# Revit family: Endpiece Linear Lightline_63_UN_Surface-Mounted-Pendant_NAL
name_source: partatom
category: Lighting Fixtures
units: mm (PartAtom-declared; Revit-internal decimal feet)

## family parameters
Always vertical = No
Cut with Voids When Loaded = No
Light Source = No
OmniClass Number = 23.80.70.00
OmniClass Title = Lighting
Part Type = Normal
Room Calculation Point = Yes
Round Connector Dimension = Use Diameter
Shared = No
Work Plane-Based = No

## types (57) — shared parameters
Apparent Load = 16 VA
Assembly Code = 63.0
Description = Surface-mounted or pendant luminaire
Geometry = Linear Lightline - Profile Geometry : Profile + Luminaire
IfcExportAs = IfcLightFixtureType
IfcExportType = USERDEFINED
Lamp = LED
Luminaire_Body_Material = PPS Plastic
Luminaire_Cap_Material = PPS Plastic
Manufacturer = Natec Lighting B.V.
Model = Linear Lightline
URL = https://nateclighting.nl
Voltage = 230 V

## per-type parameters (varying)
| type | Lightsource | Wattage Comments |
| Lighting Properties: 35W - 120° - Milky | Linear Lightline - Lightsource : Properties: 35W - 120° - Milky | 35.3391 W |
| Lighting Properties: 35W - 120° | Linear Lightline - Lightsource : Properties: 35W - 120° | 35.4575 W |
| Lighting Properties: 35W - 30° | Linear Lightline - Lightsource : Properties: 35W - 30° | 35.4382 W |
| Lighting Properties: 35W - 60° | Linear Lightline - Lightsource : Properties: 35W - 60° | 35.4888 W |
| Lighting Properties: 35W - 90°. | Linear Lightline - Lightsource : Properties: 35W - 90°. | 35.4593 W |
| Lighting Properties: 35W - Asymmetrisch | Linear Lightline - Lightsource : Properties: 35W - Asymmetrisch | 35.4371 W |
| Lighting Properties: 35W - Dubbel Asymmetrisch | Linear Lightline - Lightsource : Properties: 35W - Dubbel Asymmetrisch | 35.4449 W |
| Lighting Properties: 40W - 120° - Milky | Linear Lightline - Lightsource : Properties: 40W - 120° - Milky | 40.2837 W |
| Lighting Properties: 40W - 120° | Linear Lightline - Lightsource : Properties: 40W - 120° | 40.3964 W |
| Lighting Properties: 40W - 30° | Linear Lightline - Lightsource : Properties: 40W - 30° | 40.4281 W |
| Lighting Properties: 40W - 60° | Linear Lightline - Lightsource : Properties: 40W - 60° | 40.4582 W |
| Lighting Properties: 40W - 90° | Linear Lightline - Lightsource : Properties: 40W - 90° | 40.4791 W |
| Lighting Properties: 40W - Asymmetrisch | Linear Lightline - Lightsource : Properties: 40W - Asymmetrisch | 40.4009 W |
| Lighting Properties: 40W - Dubbel Asymmetrisch | Linear Lightline - Lightsource : Properties: 40W - Dubbel Asymmetrisch | 40.4164 W |
| Lighting Properties: 45W - 120° - Milky | Linear Lightline - Lightsource : Properties: 45W - 120° - Milky | 45.2505 W |
| Lighting Properties: 45W - 120° | Linear Lightline - Lightsource : Properties: 45W - 120° | 45.5209 W |
| Lighting Properties: 45W - 30° | Linear Lightline - Lightsource : Properties: 45W - 30° | 45.4163 W |
| Lighting Properties: 45W - 60° | Linear Lightline - Lightsource : Properties: 45W - 60° | 45.4916 W |
| Lighting Properties: 45W - 90° | Linear Lightline - Lightsource : Properties: 45W - 90° | 45.4339 W |
| Lighting Properties: 45W - Asymmetrisch | Linear Lightline - Lightsource : Properties: 45W - Asymmetrisch | 45.4889 W |
| Lighting Properties: 45W - Dubbel Asymmetrisch | Linear Lightline - Lightsource : Properties: 45W - Dubbel Asymmetrisch | 45.4156 W |
| Lighting Properties: 50W - 120° - Milky | Linear Lightline - Lightsource : Properties: 50W - 120° - Milky | 50.7982 W |
| Lighting Properties: 50W - 120° | Linear Lightline - Lightsource : Properties: 50W - 120° | 50.9088 W |
| Lighting Properties: 50W - 30° | Linear Lightline - Lightsource : Properties: 50W - 30° | 50.9496 W |
| Lighting Properties: 50W - 60° | Linear Lightline - Lightsource : Properties: 50W - 60° | 50.9299 W |
| Lighting Properties: 50W - 90° | Linear Lightline - Lightsource : Properties: 50W - 90° | 50.9461 W |
| Lighting Properties: 50W - Asymmetrisch | Linear Lightline - Lightsource : Properties: 50W - Asymmetrisch | 50.9791 W |
| Lighting Properties: 50W - Dubbel Asymmetrisch | Linear Lightline - Lightsource : Properties: 50W - Dubbel Asymmetrisch | 50.9462 W |
| Lighting Properties: 55W - 120° - Milky | Linear Lightline - Lightsource : Properties: 55W - 120° - Milky | 54.7339 W |
| Lighting Properties: 55W - 120° | Linear Lightline - Lightsource : Properties: 55W - 120° | 54.7819 W |
| Lighting Properties: 55W - 30° | Linear Lightline - Lightsource : Properties: 55W - 30° | 54.7371 W |
| Lighting Properties: 55W - 60° | Linear Lightline - Lightsource : Properties: 55W - 60° | 54.8068 W |
| Lighting Properties: 55W - 90° | Linear Lightline - Lightsource : Properties: 55W - 90° | 54.8356 W |
| Lighting Properties: 55W - Asymmetrisch | Linear Lightline - Lightsource : Properties: 55W - Asymmetrisch | 54.74 W |
| Lighting Properties: 55W - Dubbel Asymmetrisch | Linear Lightline - Lightsource : Properties: 55W - Dubbel Asymmetrisch | 54.7224 W |
| Lighting Properties: 60W - 120° - Milky | Linear Lightline - Lightsource : Properties: 60W - 120° - Milky | 59.9828 W |
| Lighting Properties: 60W - 120° | Linear Lightline - Lightsource : Properties: 60W - 120° | 59.9186 W |
| Lighting Properties: 60W - 30° | Linear Lightline - Lightsource : Properties: 60W - 30° | 59.8252 W |
| Lighting Properties: 60W - 60° | Linear Lightline - Lightsource : Properties: 60W - 60° | 60.0322 W |
| Lighting Properties: 60W - 90° | Linear Lightline - Lightsource : Properties: 60W - 90° | 59.9012 W |
| Lighting Properties: 60W - Asymmetrisch | Linear Lightline - Lightsource : Properties: 60W - Asymmetrisch | 59.8559 W |
| Lighting Properties: 60W - Dubbel Asymmetrisch | Linear Lightline - Lightsource : Properties: 60W - Dubbel Asymmetrisch | 59.768 W |
| Lighting Properties: 65W - 120° - Milky | Linear Lightline - Lightsource : Properties: 65W - 120° - Milky | 64.9414 W |
| Lighting Properties: 65W - 120° | Linear Lightline - Lightsource : Properties: 65W - 120° | 64.9257 W |
| Lighting Properties: 65W - 30° | Linear Lightline - Lightsource : Properties: 65W - 30° | 64.9077 W |
| Lighting Properties: 65W - 60° | Linear Lightline - Lightsource : Properties: 65W - 60° | 64.9068 W |
| Lighting Properties: 65W - 90° | Linear Lightline - Lightsource : Properties: 65W - 90° | 64.9996 W |
| Lighting Properties: 65W - Asymmetrisch | Linear Lightline - Lightsource : Properties: 65W - Asymmetrisch | 64.8497 W |
| Lighting Properties: 65W - Dubbel Asymmetrisch | Linear Lightline - Lightsource : Properties: 65W - Dubbel Asymmetrisch | 64.8665 W |
| Lighting Properties: 70W - 120° - Milky | Linear Lightline - Lightsource : Properties: 70W - 120° - Milky | 70.8849 W |
| Lighting Properties: 70W - 120° | Linear Lightline - Lightsource : Properties: 70W - 120° | 70.8736 W |
| Lighting Properties: 70W - 30° | Linear Lightline - Lightsource : Properties: 70W - 30° | 70.7391 W |
| Lighting Properties: 70W - 60° | Linear Lightline - Lightsource : Properties: 70W - 60° | 70.8531 W |
| Lighting Properties: 70W - 90° - NV | Linear Lightline - Lightsource : Properties: 70W - 90° - NV | 70.8166 W |
| Lighting Properties: 70W - 90° | Linear Lightline - Lightsource : Properties: 70W - 90° | 70.8166 W |
| Lighting Properties: 70W - Asymmetrisch | Linear Lightline - Lightsource : Properties: 70W - Asymmetrisch | 70.6303 W |
| Lighting Properties: 70W - Dubbel Asymmetrisch | Linear Lightline - Lightsource : Properties: 70W - Dubbel Asymmetrisch | 70.8838 W |

## geometry (parser evidence)
native form markers: Sweep x19
no freeform markers — native parametric forms only
